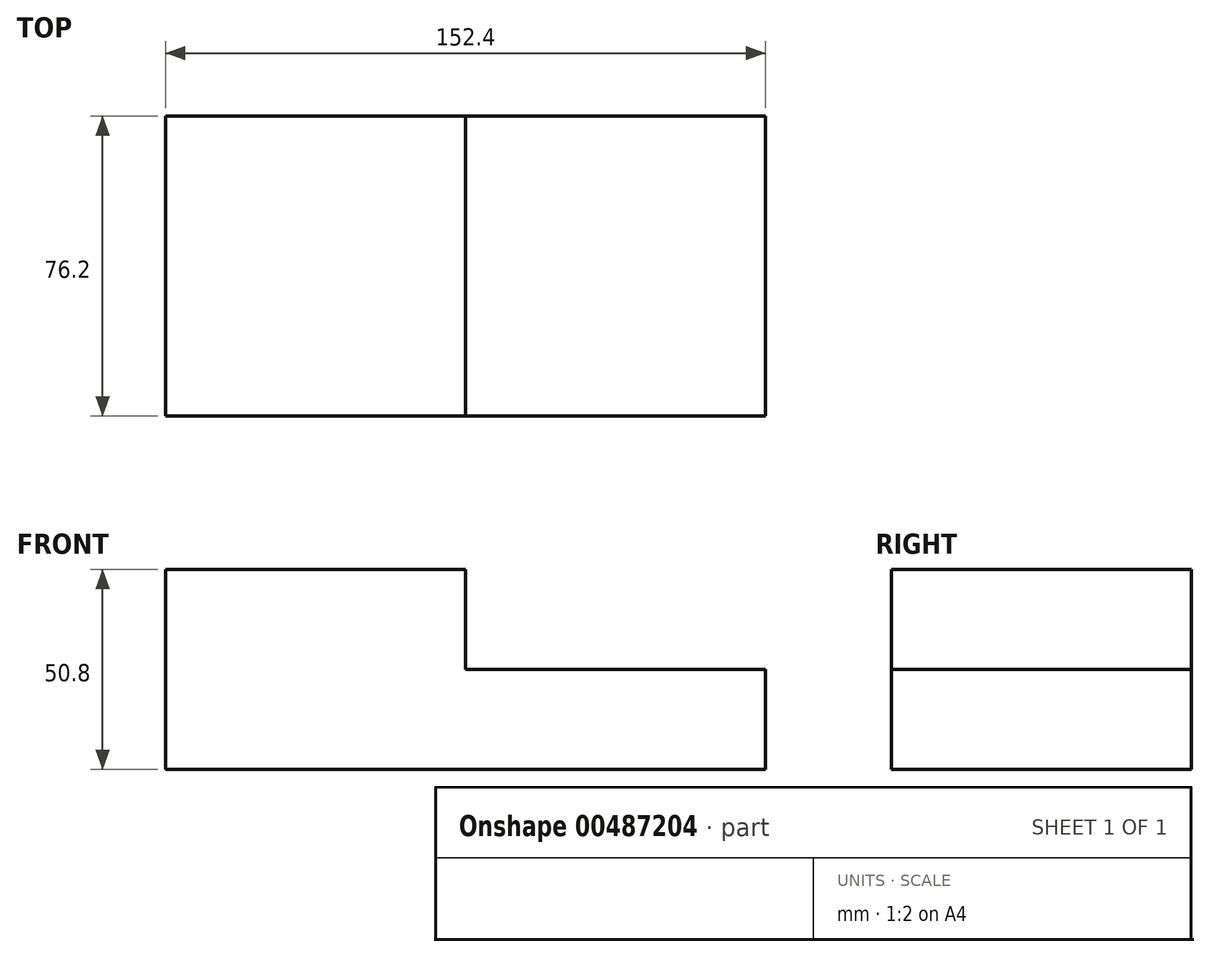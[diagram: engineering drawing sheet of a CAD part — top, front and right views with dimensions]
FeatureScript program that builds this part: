
annotation { "Feature Type Name" : "Feature", "Feature Type Description" : "" }
export const myFeature = defineFeature(function(context is Context, id is Id, definition is map)
    precondition{}
    {
        {
            var Q0;
            Q0=qCreatedBy(makeId("Front.planeOp"),FACE);
            var sketch = newSketch(context, id + "F0", { "sketchPlane" : qUnion([Q0])});
            skLineSegment(sketch, "E0", {"start": v(-76.67, 68.64) * mm, "end": v(-0.47, 68.64) * mm});
            skLineSegment(sketch, "E1", {"start": v(-0.47, 68.64) * mm, "end": v(-0.47, 43.24) * mm});
            skLineSegment(sketch, "E2", {"start": v(-0.47, 43.24) * mm, "end": v(75.73, 43.24) * mm});
            skLineSegment(sketch, "E3", {"start": v(75.73, 43.24) * mm, "end": v(75.73, 17.84) * mm});
            skLineSegment(sketch, "E4", {"start": v(75.73, 17.84) * mm, "end": v(-76.67, 17.84) * mm});
            skLineSegment(sketch, "E5", {"start": v(-76.67, 17.84) * mm, "end": v(-76.67, 68.64) * mm});
            skSolve(sketch);
        }
        {
            var Q0;
            Q0=makeQuery(id+"F0.imprint","IMPRINT",FACE,{"disambiguationData":[TD([[makeQuery(id+"F0.imprint","IMPRINT",EDGE,{"derivedFrom":sQuery(id+"F0.wireOp",EDGE,"E0")}),-1.0]])]});
            extrude(context, id + "F1", {"entities" : qUnion([Q0]), "depth" : 76.2 * mm});
        }
    });
